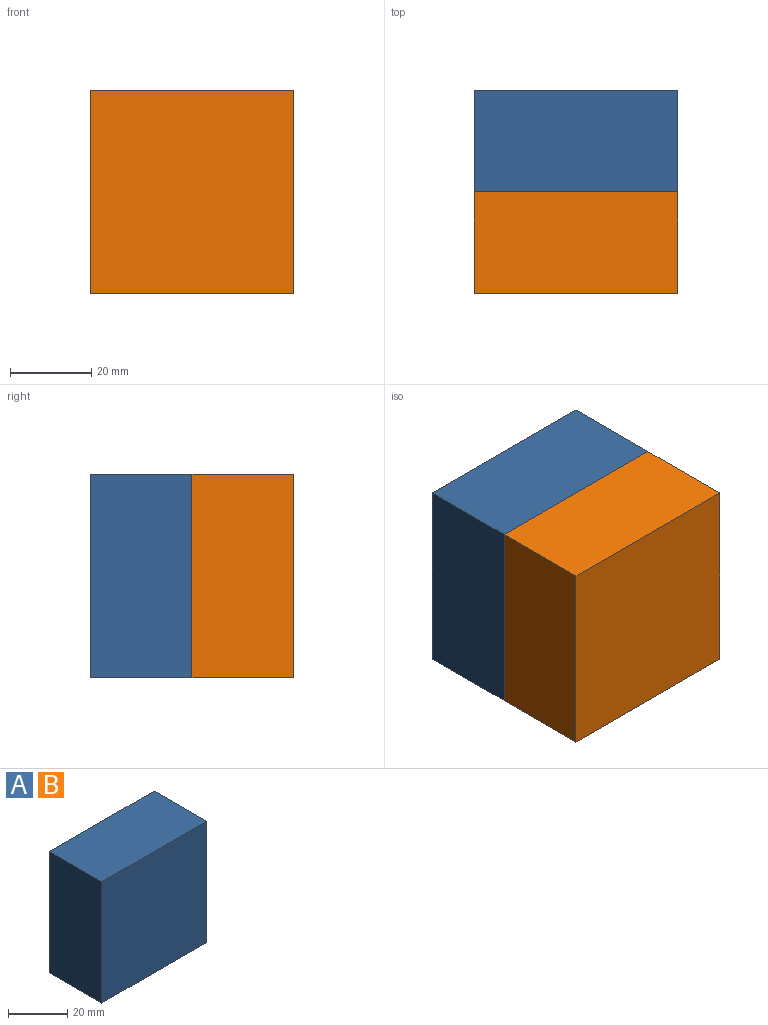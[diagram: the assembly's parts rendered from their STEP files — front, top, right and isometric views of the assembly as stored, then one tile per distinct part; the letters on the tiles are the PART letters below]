
ASSEMBLY  parts=2 mates=1
PART A: 6 faces, bbox 50x25x50 mm
  f0: plane 50x25mm, normal (-1,0,0), area 1250mm2, adj f1,f3,f4,f5
  f1: plane 50x25mm, normal (0,0,-1), area 1250mm2, adj f0,f2,f4,f5
  f2: plane 50x25mm, normal (1,0,0), area 1250mm2, adj f1,f3,f4,f5
  f3: plane 50x25mm, normal (0,0,1), area 1250mm2, adj f0,f2,f4,f5
  f4: plane 50x50mm, normal (0,-1,0), area 2500mm2, adj f0,f1,f2,f3
  f5: plane 50x50mm, normal (0,1,0), area 2500mm2, adj f0,f1,f2,f3
PART B: same geometry as A
PLACE A t=(-92.83,-40.18,-36.12)mm
PLACE B t=(-92.83,-65.18,-36.12)mm
MATE revolute A.f4 <-> B.f5  axis (0,-1,0) through (-92.83,-65.18,-36.12)mm
